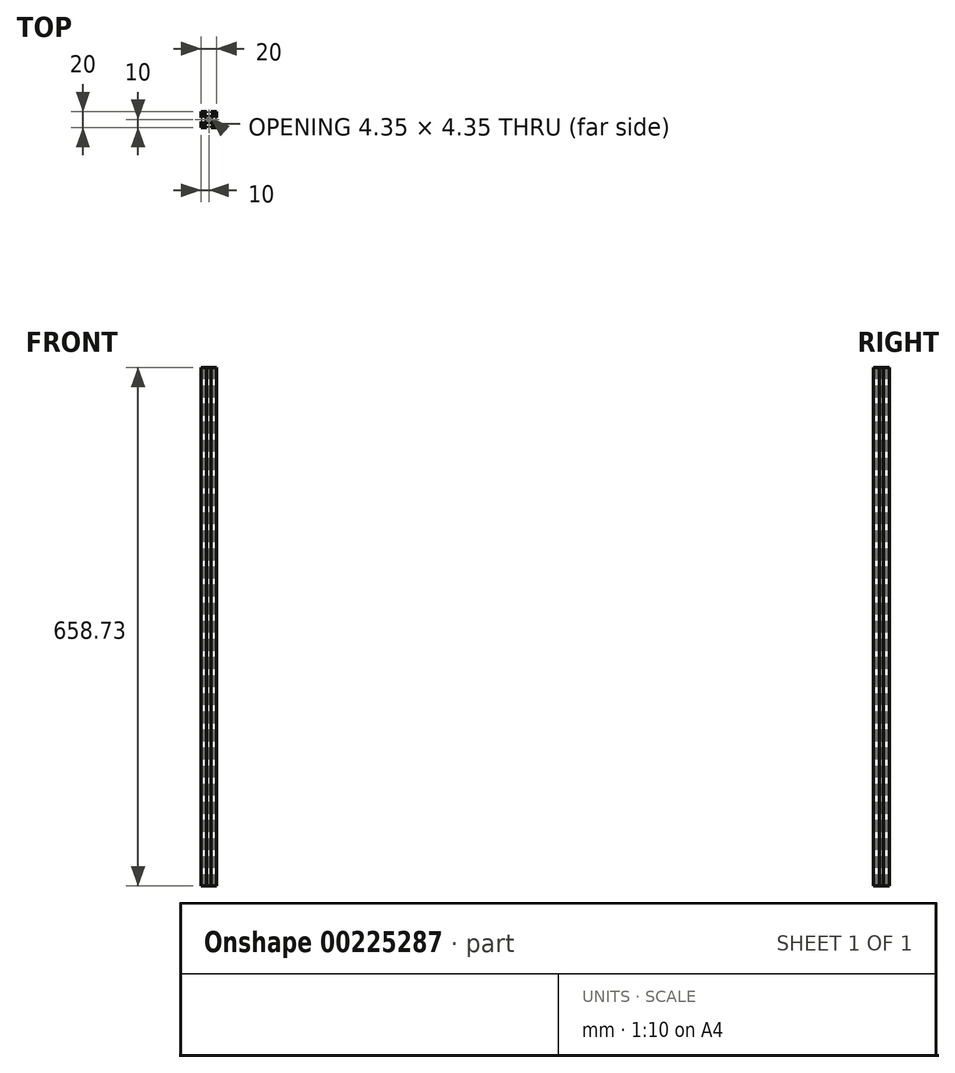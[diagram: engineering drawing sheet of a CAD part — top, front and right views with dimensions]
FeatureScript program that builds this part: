
annotation { "Feature Type Name" : "Feature", "Feature Type Description" : "" }
export const myFeature = defineFeature(function(context is Context, id is Id, definition is map)
    precondition{}
    {
        {
            var Q0;
            Q0=qCreatedBy(makeId("Top.planeOp"),FACE);
            var sketch = newSketch(context, id + "F0", { "sketchPlane" : qUnion([Q0])});
            skLineSegment(sketch, "E0.bottom", {"start": v(10, 10) * mm, "end": v(-10, 10) * mm});
            skLineSegment(sketch, "E0.top", {"start": v(10, -10) * mm, "end": v(-10, -10) * mm});
            skLineSegment(sketch, "E0.left", {"start": v(10, 10) * mm, "end": v(10, -10) * mm});
            skLineSegment(sketch, "E0.right", {"start": v(-10, 10) * mm, "end": v(-10, -10) * mm});
            skPoint(sketch, "E0.middle", {"position": v(0, 0) * mm});
            skLineSegment(sketch, "E1", {"start": v(-10, 10) * mm, "end": v(10, -10) * mm, "construction": true});
            skLineSegment(sketch, "E2", {"start": v(-10, -10) * mm, "end": v(10, 10) * mm, "construction": true});
            skLineSegment(sketch, "E3", {"start": v(0, 10) * mm, "end": v(0, -10) * mm, "construction": true});
            skLineSegment(sketch, "E4", {"start": v(-10, 0) * mm, "end": v(10, 0) * mm, "construction": true});
            skPoint(sketch, "E4.endSnap0", {"position": v(10, 0) * mm});
            skLineSegment(sketch, "E5", {"start": v(-2.63, 13.49) * mm, "end": v(2.63, 13.49) * mm});
            skLineSegment(sketch, "E6", {"start": v(2.63, 13.49) * mm, "end": v(2.63, 8.5) * mm});
            skLineSegment(sketch, "E7", {"start": v(2.63, 8.5) * mm, "end": v(6, 8.5) * mm});
            skLineSegment(sketch, "E8", {"start": v(6, 8.5) * mm, "end": v(6, 7.06) * mm});
            skLineSegment(sketch, "E9", {"start": v(6, 7.06) * mm, "end": v(2.6, 3.66) * mm});
            skLineSegment(sketch, "E10", {"start": v(2.6, 3.66) * mm, "end": v(-2.6, 3.66) * mm});
            skLineSegment(sketch, "E11", {"start": v(-2.6, 3.66) * mm, "end": v(-6, 7.06) * mm});
            skLineSegment(sketch, "E12", {"start": v(-6, 7.06) * mm, "end": v(-6, 8.5) * mm});
            skLineSegment(sketch, "E13", {"start": v(-6, 8.5) * mm, "end": v(-2.63, 8.5) * mm});
            skLineSegment(sketch, "E14", {"start": v(-2.63, 8.5) * mm, "end": v(-2.63, 13.49) * mm});
            skCircle(sketch, "E15", {"center": v(0, 0) * mm, "radius": 2.1 * mm});
            skLineSegment(sketch, "E16.MirrorCS", {"start": v(-7.06, 6) * mm, "end": v(-8.5, 6) * mm});
            skLineSegment(sketch, "E17.MirrorCS", {"start": v(-3.66, 2.6) * mm, "end": v(-7.06, 6) * mm});
            skLineSegment(sketch, "E18.MirrorCS", {"start": v(-8.5, 6) * mm, "end": v(-8.5, 2.63) * mm});
            skLineSegment(sketch, "E19.MirrorCS", {"start": v(-3.66, -2.6) * mm, "end": v(-3.66, 2.6) * mm});
            skLineSegment(sketch, "E20.MirrorCS", {"start": v(-7.06, -6) * mm, "end": v(-3.66, -2.6) * mm});
            skLineSegment(sketch, "E21.MirrorCS", {"start": v(-8.5, -6) * mm, "end": v(-7.06, -6) * mm});
            skLineSegment(sketch, "E22.MirrorCS", {"start": v(-8.5, -2.63) * mm, "end": v(-8.5, -6) * mm});
            skLineSegment(sketch, "E23.MirrorCS", {"start": v(-13.49, -2.63) * mm, "end": v(-8.5, -2.63) * mm});
            skLineSegment(sketch, "E24.MirrorCS", {"start": v(-13.49, 2.63) * mm, "end": v(-13.49, -2.63) * mm});
            skLineSegment(sketch, "E25.MirrorCS", {"start": v(-8.5, 2.63) * mm, "end": v(-13.49, 2.63) * mm});
            skLineSegment(sketch, "E26.MirrorCS", {"start": v(-2.6, -3.66) * mm, "end": v(-6, -7.06) * mm});
            skLineSegment(sketch, "E27.MirrorCS", {"start": v(2.6, -3.66) * mm, "end": v(-2.6, -3.66) * mm});
            skLineSegment(sketch, "E28.MirrorCS", {"start": v(6, -7.06) * mm, "end": v(2.6, -3.66) * mm});
            skLineSegment(sketch, "E29.MirrorCS", {"start": v(6, -8.5) * mm, "end": v(6, -7.06) * mm});
            skLineSegment(sketch, "E30.MirrorCS", {"start": v(2.63, -8.5) * mm, "end": v(6, -8.5) * mm});
            skLineSegment(sketch, "E31.MirrorCS", {"start": v(2.63, -13.49) * mm, "end": v(2.63, -8.5) * mm});
            skLineSegment(sketch, "E32.MirrorCS", {"start": v(-2.63, -13.49) * mm, "end": v(2.63, -13.49) * mm});
            skLineSegment(sketch, "E33.MirrorCS", {"start": v(-2.63, -8.5) * mm, "end": v(-2.63, -13.49) * mm});
            skLineSegment(sketch, "E34.MirrorCS", {"start": v(-6, -8.5) * mm, "end": v(-2.63, -8.5) * mm});
            skLineSegment(sketch, "E35.MirrorCS", {"start": v(-6, -7.06) * mm, "end": v(-6, -8.5) * mm});
            skLineSegment(sketch, "E36.MirrorCS", {"start": v(7.06, 6) * mm, "end": v(3.66, 2.6) * mm});
            skLineSegment(sketch, "E37.MirrorCS", {"start": v(8.5, 6) * mm, "end": v(7.06, 6) * mm});
            skLineSegment(sketch, "E38.MirrorCS", {"start": v(8.5, 2.63) * mm, "end": v(8.5, 6) * mm});
            skLineSegment(sketch, "E39.MirrorCS", {"start": v(13.49, 2.63) * mm, "end": v(8.5, 2.63) * mm});
            skLineSegment(sketch, "E40.MirrorCS", {"start": v(13.49, -2.63) * mm, "end": v(13.49, 2.63) * mm});
            skLineSegment(sketch, "E41.MirrorCS", {"start": v(8.5, -2.63) * mm, "end": v(13.49, -2.63) * mm});
            skLineSegment(sketch, "E42.MirrorCS", {"start": v(8.5, -6) * mm, "end": v(8.5, -2.63) * mm});
            skLineSegment(sketch, "E43.MirrorCS", {"start": v(7.06, -6) * mm, "end": v(8.5, -6) * mm});
            skLineSegment(sketch, "E44.MirrorCS", {"start": v(3.66, -2.6) * mm, "end": v(7.06, -6) * mm});
            skLineSegment(sketch, "E45.MirrorCS", {"start": v(3.66, 2.6) * mm, "end": v(3.66, -2.6) * mm});
            skCircle(sketch, "E46", {"center": v(-1.48, 1.48) * mm, "radius": 0.7 * mm});
            skCircle(sketch, "E47.MirrorC", {"center": v(1.48, 1.48) * mm, "radius": 0.7 * mm});
            skCircle(sketch, "E48.MirrorC", {"center": v(-1.48, -1.48) * mm, "radius": 0.7 * mm});
            skCircle(sketch, "E49.MirrorC", {"center": v(1.48, -1.48) * mm, "radius": 0.7 * mm});
            skSolve(sketch);
        }
        {
            var Q0;
            {var subQ29=sQuery(id+"F0.wireOp",EDGE,"E7");Q0=makeQuery(id+"F0.imprint","IMPRINT",FACE,{"disambiguationData":[TD([[makeQuery(id+"F0.imprint","IMPRINT",EDGE,{"derivedFrom":subQ29}),1.0]])]});}
            extrude(context, id + "F1", {"entities" : qUnion([Q0]), "depth" : 658.73 * mm});
        }
    });
